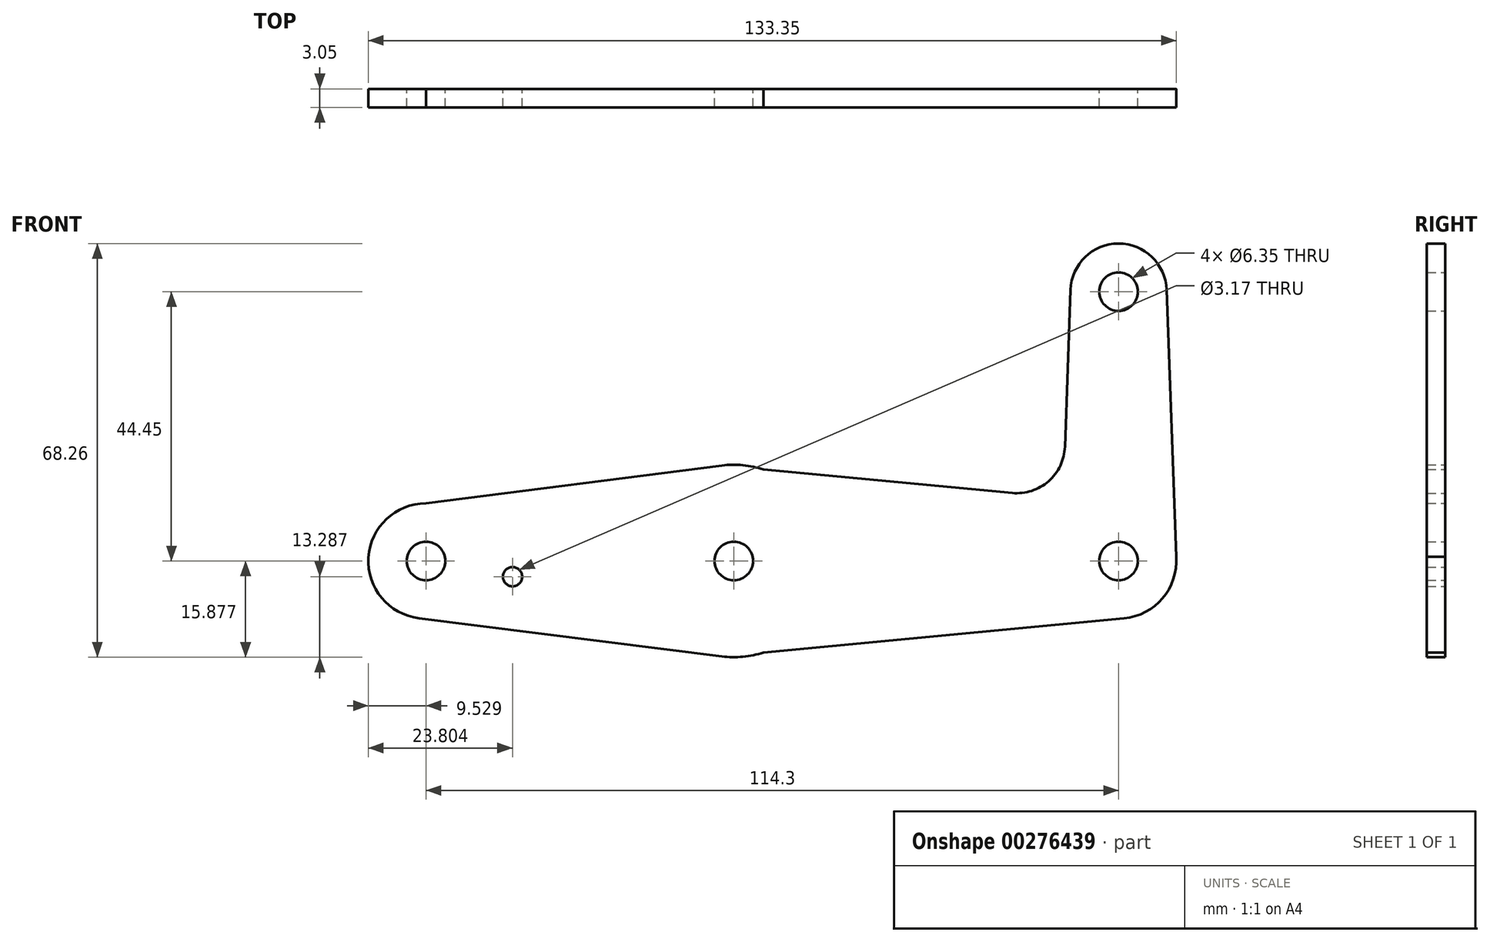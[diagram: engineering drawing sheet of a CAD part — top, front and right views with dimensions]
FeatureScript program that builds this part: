
annotation { "Feature Type Name" : "Feature", "Feature Type Description" : "" }
export const myFeature = defineFeature(function(context is Context, id is Id, definition is map)
    precondition{}
    {
        {
            var Q0;
            Q0=qCreatedBy(makeId("Front.planeOp"),FACE);
            var sketch = newSketch(context, id + "F0", { "sketchPlane" : qUnion([Q0])});
            skLineSegment(sketch, "E0", {"start": v(-46.22, -31.08) * mm, "end": v(68.08, -31.08) * mm});
            skCircle(sketch, "E1", {"center": v(-46.22, -31.08) * mm, "radius": 9.53 * mm});
            skCircle(sketch, "E2", {"center": v(68.08, -31.08) * mm, "radius": 9.53 * mm});
            skLineSegment(sketch, "E3", {"start": v(-46.22, -31.08) * mm, "end": v(4.58, -31.08) * mm});
            skCircle(sketch, "E4", {"center": v(4.58, -31.08) * mm, "radius": 15.88 * mm});
            skLineSegment(sketch, "E5", {"start": v(68.08, -31.08) * mm, "end": v(68.08, 13.37) * mm});
            skCircle(sketch, "E6", {"center": v(68.08, 13.37) * mm, "radius": 7.94 * mm});
            skLineSegment(sketch, "E7", {"start": v(-47.45, -40.53) * mm, "end": v(2.6, -46.83) * mm});
            skLineSegment(sketch, "E8", {"start": v(2.6, -46.83) * mm, "end": v(68.97, -40.57) * mm});
            skLineSegment(sketch, "E9", {"start": v(-46.22, -21.56) * mm, "end": v(2.6, -15.33) * mm});
            skLineSegment(sketch, "E10", {"start": v(2.6, -15.33) * mm, "end": v(26.3, -17.57) * mm});
            skLineSegment(sketch, "E11", {"start": v(59.2, -12.67) * mm, "end": v(59.23, -12.23) * mm});
            skLineSegment(sketch, "E12", {"start": v(77.6, -31.08) * mm, "end": v(76.01, 13.65) * mm});
            skCircle(sketch, "E13", {"center": v(-46.22, -31.08) * mm, "radius": 3.18 * mm});
            skCircle(sketch, "E14", {"center": v(4.58, -31.08) * mm, "radius": 3.18 * mm});
            skCircle(sketch, "E15", {"center": v(68.08, -31.08) * mm, "radius": 3.18 * mm});
            skCircle(sketch, "E16", {"center": v(68.08, 13.37) * mm, "radius": 3.18 * mm});
            skLineSegment(sketch, "E17", {"start": v(4.58, -31.08) * mm, "end": v(-56.99, -31.08) * mm});
            skLineSegment(sketch, "E18", {"start": v(4.58, -31.08) * mm, "end": v(-31.95, -31.08) * mm});
            skLineSegment(sketch, "E19", {"start": v(26.3, -17.57) * mm, "end": v(50.53, -19.86) * mm});
            skLineSegment(sketch, "E20", {"start": v(59.2, -12.67) * mm, "end": v(60.15, 13.65) * mm});
            skCircle(sketch, "E21", {"center": v(-31.95, -33.67) * mm, "radius": 1.59 * mm});
            skPoint(sketch, "E22.newPointA", {"position": v(58.55, -31.08) * mm});
            skArc(sketch, "E22.filletArc", {"start": v(50.53, -19.86) * mm, "mid": v(56.53, -17.92) * mm, "end": v(59.23, -12.23) * mm});
            skSolve(sketch);
        }
        {
            var Q0;
            Q0 = qSketchRegion(id + "F0", true);
            var Q1;
            {var subQ0=sQuery(id+"F0.wireOp",EDGE,"E2");var subQ1=sQuery(id+"F0.wireOp",EDGE,"E0");var subQ2=makeQuery(id+"F0.imprint","INTERSECT",VERTEX,{"derivedFrom":[subQ1,subQ0]});Q1=makeQuery(id+"F0.imprint","IMPRINT",FACE,{"disambiguationData":[TD([[makeQuery(id+"F0.imprint","IMPRINT",EDGE,{"disambiguationData":[TD([[subQ2,-1.0]])],"derivedFrom":subQ1}),1.0]])]});}
            extrude(context, id + "F1", {"entities" : qUnion([Q0, Q1]), "depth" : 3.05 * mm});
        }
    });
